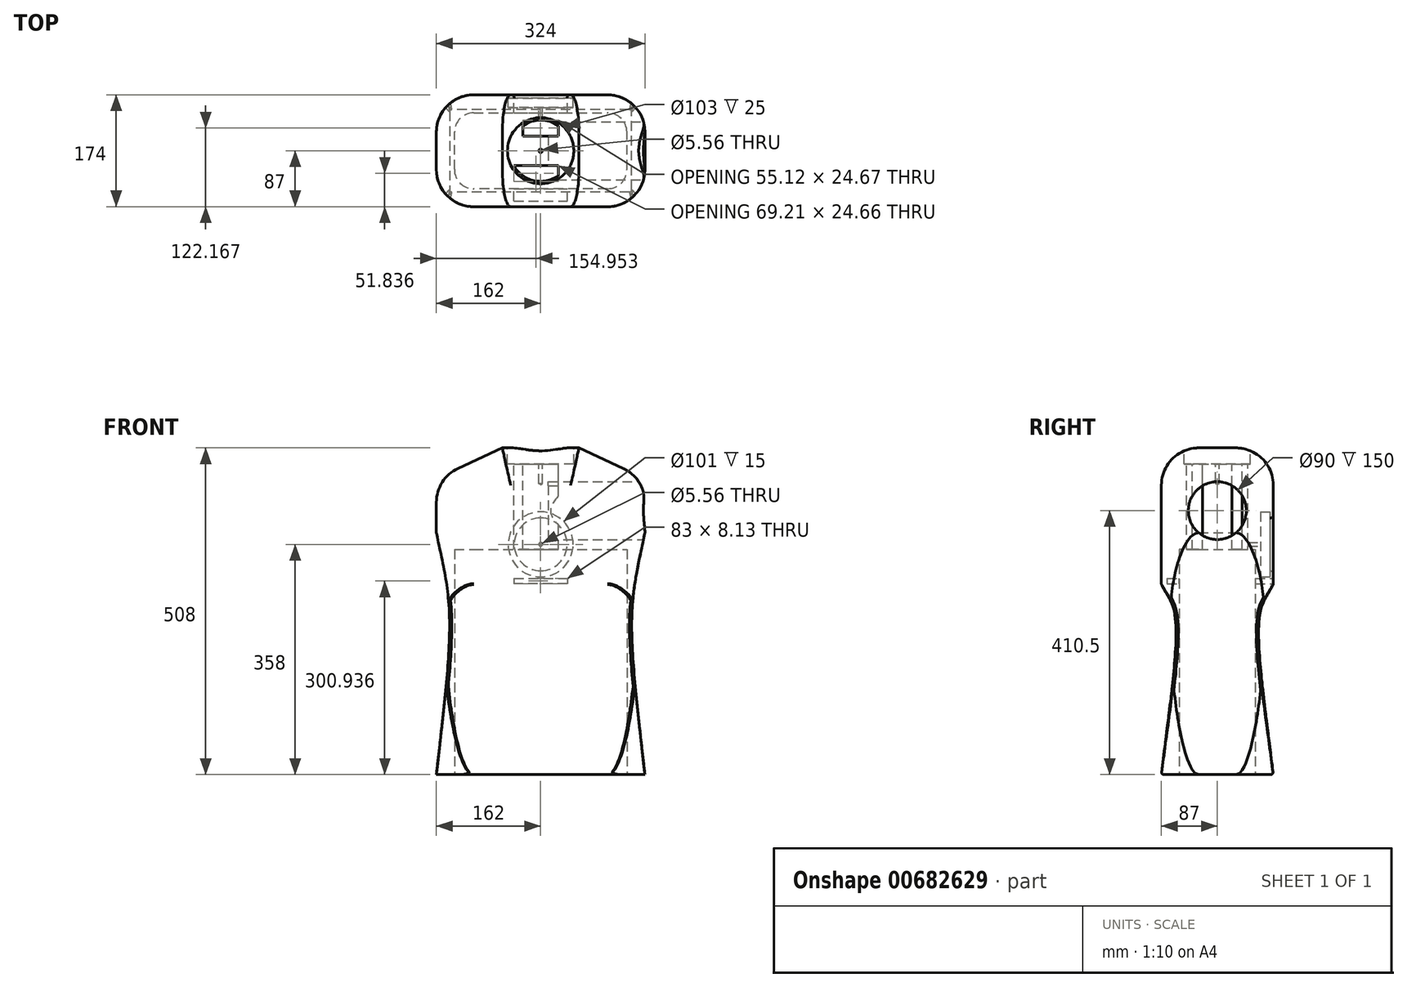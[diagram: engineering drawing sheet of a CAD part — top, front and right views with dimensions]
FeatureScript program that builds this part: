
annotation { "Feature Type Name" : "Feature", "Feature Type Description" : "" }
export const myFeature = defineFeature(function(context is Context, id is Id, definition is map)
    precondition{}
    {
        {
            var Q0;
            Q0=qCreatedBy(makeId("Front.planeOp"),FACE);
            var sketch = newSketch(context, id + "F0", { "sketchPlane" : qUnion([Q0])});
            skLineSegment(sketch, "E0.bottom", {"start": v(162, 254) * mm, "end": v(-162, 254) * mm});
            skLineSegment(sketch, "E0.top", {"start": v(162, -254) * mm, "end": v(-162, -254) * mm});
            skLineSegment(sketch, "E0.left", {"start": v(162, 254) * mm, "end": v(162, -254) * mm});
            skLineSegment(sketch, "E0.right", {"start": v(-162, 254) * mm, "end": v(-162, -254) * mm});
            skPoint(sketch, "E0.middle", {"position": v(0, 0) * mm});
            skSolve(sketch);
        }
        {
            var Q0;
            Q0=makeQuery(id+"F0.imprint","IMPRINT",FACE,{"disambiguationData":[TD([[makeQuery(id+"F0.imprint","IMPRINT",EDGE,{"derivedFrom":sQuery(id+"F0.wireOp",EDGE,"E0.bottom")}),1.0]])]});
            extrude(context, id + "F1", {"entities" : qUnion([Q0]), "depth" : 87 * mm, "offsetDistance" : 25 * mm, "hasSecondDirection" : true, "secondDirectionOppositeDirection" : true, "secondDirectionDepth" : 87 * mm});
        }
        {
            var Q0;
            Q0=makeQuery(id+"F1.opExtrude","SWEPT_FACE",FACE,{"disambiguationData":[OSD([sQuery(id+"F0.wireOp",EDGE,"E0.bottom")])]});
            var sketch = newSketch(context, id + "F2", { "sketchPlane" : qUnion([Q0])});
            skCircle(sketch, "E1", {"center": v(0, 0) * mm, "radius": 51.5 * mm});
            skPoint(sketch, "E1.centerSnap0", {"position": v(-162, 0) * mm});
            skPoint(sketch, "E1.centerSnap1", {"position": v(0, 87) * mm});
            skSolve(sketch);
        }
        {
            var Q0;
            Q0=makeQuery(id+"F2.imprint","IMPRINT",FACE,{"disambiguationData":[TD([[makeQuery(id+"F2.imprint","IMPRINT",EDGE,{"derivedFrom":sQuery(id+"F2.wireOp",EDGE,"E1")}),1.0]])]});
            extrude(context, id + "F3", {"entities" : qUnion([Q0]), "operationType" : NewBodyOperationType.REMOVE, "oppositeDirection" : true, "depth" : 25 * mm, "offsetDistance" : 25 * mm});
        }
        {
            var Q0;
            Q0=makeQuery(id+"F3.boolean.opBoolean","COPY",FACE,{"derivedFrom":makeQuery(id+"F3.opExtrude","CAP_FACE",FACE,{"disambiguationData":[OSD([sQuery(id+"F2.wireOp",EDGE,"E1")])],"isStart":false})});
            var sketch = newSketch(context, id + "F4", { "sketchPlane" : qUnion([Q0])});
            skCircle(sketch, "E2.0.0", {"center": v(0, 0) * mm, "radius": 51.5 * mm});
            skCircle(sketch, "E3", {"center": v(0, 0) * mm, "radius": 3.17 * mm});
            skSolve(sketch);
        }
        {
            var Q0;
            Q0=sQuery(id+"F4.wireOp",VERTEX,"E2.0.0.center");
            var Q1;
            Q1=makeQuery(id+"F1.opExtrude","SWEPT_BODY",BODY,{"disambiguationData":[OSD([sQuery(id+"F0.wireOp",EDGE,"E0.bottom"),sQuery(id+"F0.wireOp",EDGE,"E0.top"),sQuery(id+"F0.wireOp",EDGE,"E0.left"),sQuery(id+"F0.wireOp",EDGE,"E0.right")])]});
            hole(context, id + "F5", {"style" : HoleStyle.SIMPLE, "endStyle" : HoleEndStyle.BLIND, "standardTappedOrClearance" : lookupTablePath({ "standard" : "ANSI", "engagement" : "50%", "pitch" : "20 tpi", "size" : "1/4", "type" : "Tapped" }), "standardBlindInLast" : lookupTablePath({ "standard" : "ANSI", "engagement" : "50%", "pitch" : "20 tpi", "size" : "1/4", "type" : "Tapped" }), "holeDiameter" : 5.56 * mm, "majorDiameter" : 6.35 * mm, "showTappedDepth" : true, "holeDepth" : 30.48 * mm, "isTappedThrough" : true, "tappedDepth" : 25.4 * mm, "tapClearance" : 4, "locations" : qUnion([Q0]), "scope" : qUnion([Q1])});
        }
        {
            var Q0;
            Q0=makeQuery(id+"F1.opExtrude","SWEPT_EDGE",EDGE,{"disambiguationData":[OSD([sQuery(id+"F0.wireOp",EDGE,"E0.bottom"),sQuery(id+"F0.wireOp",EDGE,"E0.right")])]});
            var Q1;
            Q1=makeQuery(id+"F1.opExtrude","SWEPT_EDGE",EDGE,{"disambiguationData":[OSD([sQuery(id+"F0.wireOp",EDGE,"E0.bottom"),sQuery(id+"F0.wireOp",EDGE,"E0.left")])]});
            chamfer(context, id + "F6", {"entities" : qUnion([Q0, Q1]), "chamferType" : ChamferType.TWO_OFFSETS, "width1" : 47.5 * mm, "oppositeDirection" : false, "width2" : 102.5 * mm, "tangentPropagation" : true});
        }
        {
            var Q0;
            Q0=makeQuery(id+"F6.opChamfer","BLEND_FACE",FACE,{"disambiguationData":[OSD([sQuery(id+"F0.wireOp",EDGE,"E0.bottom"),sQuery(id+"F0.wireOp",EDGE,"E0.left")])]});
            var sketch = newSketch(context, id + "F7", { "sketchPlane" : qUnion([Q0])});
            skLineSegment(sketch, "E4.0.0", {"start": v(-52.81, -87) * mm, "end": v(60.16, -87) * mm});
            skLineSegment(sketch, "E4.0.1", {"start": v(60.16, -87) * mm, "end": v(60.16, 87) * mm});
            skLineSegment(sketch, "E4.0.2", {"start": v(60.16, 87) * mm, "end": v(-52.81, 87) * mm});
            skLineSegment(sketch, "E4.0.3", {"start": v(-52.81, 87) * mm, "end": v(-52.81, -87) * mm});
            skSolve(sketch);
        }
        {
            var Q0;
            {var subQ0=sQuery(id+"F0.wireOp",EDGE,"E0.right");var subQ1=sQuery(id+"F0.wireOp",EDGE,"E0.bottom");Q0=makeQuery(id+"F6.opChamfer","BLEND_EDGE",EDGE,{"blendedFrom":[makeQuery(id+"F1.opExtrude","SWEPT_EDGE",EDGE,{"disambiguationData":[OSD([subQ1,subQ0])]}),makeQuery(id+"F1.opExtrude","CAP_FACE",FACE,{"disambiguationData":[OSD([subQ1,sQuery(id+"F0.wireOp",EDGE,"E0.top"),sQuery(id+"F0.wireOp",EDGE,"E0.left"),subQ0])],"isStart":false})],"blendedInto":[makeQuery(id+"F1.opExtrude","CAP_FACE",FACE,{"disambiguationData":[OSD([subQ1,sQuery(id+"F0.wireOp",EDGE,"E0.top"),sQuery(id+"F0.wireOp",EDGE,"E0.left"),subQ0])],"isStart":false})]});}
            var Q1;
            Q1=makeQuery(id+"F1.opExtrude","CAP_EDGE",EDGE,{"disambiguationData":[OSD([sQuery(id+"F0.wireOp",EDGE,"E0.bottom")])],"isStart":false});
            var Q2;
            {var subQ0=sQuery(id+"F0.wireOp",EDGE,"E0.left");var subQ1=sQuery(id+"F0.wireOp",EDGE,"E0.bottom");Q2=makeQuery(id+"F6.opChamfer","BLEND_EDGE",EDGE,{"blendedFrom":[makeQuery(id+"F1.opExtrude","SWEPT_EDGE",EDGE,{"disambiguationData":[OSD([subQ1,subQ0])]}),makeQuery(id+"F1.opExtrude","CAP_FACE",FACE,{"disambiguationData":[OSD([subQ1,sQuery(id+"F0.wireOp",EDGE,"E0.top"),subQ0,sQuery(id+"F0.wireOp",EDGE,"E0.right")])],"isStart":false})],"blendedInto":[makeQuery(id+"F1.opExtrude","CAP_FACE",FACE,{"disambiguationData":[OSD([subQ1,sQuery(id+"F0.wireOp",EDGE,"E0.top"),subQ0,sQuery(id+"F0.wireOp",EDGE,"E0.right")])],"isStart":false})]});}
            var Q3;
            Q3=makeQuery(id+"F1.opExtrude","CAP_EDGE",EDGE,{"disambiguationData":[OSD([sQuery(id+"F0.wireOp",EDGE,"E0.bottom")])],"isStart":true});
            var Q4;
            {var subQ0=sQuery(id+"F0.wireOp",EDGE,"E0.right");var subQ1=sQuery(id+"F0.wireOp",EDGE,"E0.bottom");Q4=makeQuery(id+"F6.opChamfer","BLEND_EDGE",EDGE,{"blendedFrom":[makeQuery(id+"F1.opExtrude","SWEPT_EDGE",EDGE,{"disambiguationData":[OSD([subQ1,subQ0])]}),makeQuery(id+"F1.opExtrude","CAP_FACE",FACE,{"disambiguationData":[OSD([subQ1,sQuery(id+"F0.wireOp",EDGE,"E0.top"),sQuery(id+"F0.wireOp",EDGE,"E0.left"),subQ0])],"isStart":true})],"blendedInto":[makeQuery(id+"F1.opExtrude","CAP_FACE",FACE,{"disambiguationData":[OSD([subQ1,sQuery(id+"F0.wireOp",EDGE,"E0.top"),sQuery(id+"F0.wireOp",EDGE,"E0.left"),subQ0])],"isStart":true})]});}
            var Q5;
            {var subQ0=sQuery(id+"F0.wireOp",EDGE,"E0.left");var subQ1=sQuery(id+"F0.wireOp",EDGE,"E0.bottom");Q5=makeQuery(id+"F6.opChamfer","BLEND_EDGE",EDGE,{"blendedFrom":[makeQuery(id+"F1.opExtrude","SWEPT_EDGE",EDGE,{"disambiguationData":[OSD([subQ1,subQ0])]}),makeQuery(id+"F1.opExtrude","CAP_FACE",FACE,{"disambiguationData":[OSD([subQ1,sQuery(id+"F0.wireOp",EDGE,"E0.top"),subQ0,sQuery(id+"F0.wireOp",EDGE,"E0.right")])],"isStart":true})],"blendedInto":[makeQuery(id+"F1.opExtrude","CAP_FACE",FACE,{"disambiguationData":[OSD([subQ1,sQuery(id+"F0.wireOp",EDGE,"E0.top"),subQ0,sQuery(id+"F0.wireOp",EDGE,"E0.right")])],"isStart":true})]});}
            var Q6;
            Q6=makeQuery(id+"F1.opExtrude","CAP_EDGE",EDGE,{"disambiguationData":[OSD([sQuery(id+"F0.wireOp",EDGE,"E0.right")])],"isStart":true});
            var Q7;
            Q7=makeQuery(id+"F1.opExtrude","CAP_EDGE",EDGE,{"disambiguationData":[OSD([sQuery(id+"F0.wireOp",EDGE,"E0.right")])],"isStart":false});
            var Q8;
            {var subQ0=sQuery(id+"F0.wireOp",EDGE,"E0.right");Q8=makeQuery(id+"F6.opChamfer","BLEND_EDGE",EDGE,{"blendedFrom":[makeQuery(id+"F1.opExtrude","SWEPT_EDGE",EDGE,{"disambiguationData":[OSD([sQuery(id+"F0.wireOp",EDGE,"E0.bottom"),subQ0])]}),makeQuery(id+"F1.opExtrude","SWEPT_FACE",FACE,{"disambiguationData":[OSD([subQ0])]})],"blendedInto":[makeQuery(id+"F1.opExtrude","SWEPT_FACE",FACE,{"disambiguationData":[OSD([subQ0])]})]});}
            var Q9;
            Q9=makeQuery(id+"F1.opExtrude","CAP_EDGE",EDGE,{"disambiguationData":[OSD([sQuery(id+"F0.wireOp",EDGE,"E0.left")])],"isStart":false});
            var Q10;
            Q10=makeQuery(id+"F1.opExtrude","CAP_EDGE",EDGE,{"disambiguationData":[OSD([sQuery(id+"F0.wireOp",EDGE,"E0.left")])],"isStart":true});
            var Q11;
            {var subQ0=sQuery(id+"F0.wireOp",EDGE,"E0.left");Q11=makeQuery(id+"F6.opChamfer","BLEND_EDGE",EDGE,{"blendedFrom":[makeQuery(id+"F1.opExtrude","SWEPT_EDGE",EDGE,{"disambiguationData":[OSD([sQuery(id+"F0.wireOp",EDGE,"E0.bottom"),subQ0])]}),makeQuery(id+"F1.opExtrude","SWEPT_FACE",FACE,{"disambiguationData":[OSD([subQ0])]})],"blendedInto":[makeQuery(id+"F1.opExtrude","SWEPT_FACE",FACE,{"disambiguationData":[OSD([subQ0])]})]});}
            fillet(context, id + "F8", {"entities" : qUnion([Q0, Q1, Q2, Q3, Q4, Q5, Q6, Q7, Q8, Q9, Q10, Q11]), "radius" : 174 * mm / 3, "tangentPropagation" : true, "allowEdgeOverflow" : false});
        }
        {
            var Q0;
            Q0=makeQuery(id+"F1.opExtrude","SWEPT_FACE",FACE,{"disambiguationData":[OSD([sQuery(id+"F0.wireOp",EDGE,"E0.left")])]});
            var sketch = newSketch(context, id + "F9", { "sketchPlane" : qUnion([Q0])});
            skCircle(sketch, "E5", {"center": v(0, 156.5) * mm, "radius": 45 * mm});
            skSolve(sketch);
        }
        {
            var Q0;
            Q0=makeQuery(id+"F9.imprint","IMPRINT",FACE,{"disambiguationData":[TD([[makeQuery(id+"F9.imprint","IMPRINT",EDGE,{"derivedFrom":sQuery(id+"F9.wireOp",EDGE,"E5")}),1.0]])]});
            extrude(context, id + "F10", {"entities" : qUnion([Q0]), "operationType" : NewBodyOperationType.REMOVE, "oppositeDirection" : true, "depth" : 150 * mm, "offsetDistance" : 25 * mm});
        }
        {
            var Q0;
            Q0=makeQuery(id+"F1.opExtrude","CAP_FACE",FACE,{"disambiguationData":[OSD([sQuery(id+"F0.wireOp",EDGE,"E0.bottom"),sQuery(id+"F0.wireOp",EDGE,"E0.top"),sQuery(id+"F0.wireOp",EDGE,"E0.left"),sQuery(id+"F0.wireOp",EDGE,"E0.right")])],"isStart":true});
            var sketch = newSketch(context, id + "F11", { "sketchPlane" : qUnion([Q0])});
            skCircle(sketch, "E6", {"center": v(0, 104) * mm, "radius": 50.5 * mm});
            skSolve(sketch);
        }
        {
            var Q0;
            Q0=makeQuery(id+"F11.imprint","IMPRINT",FACE,{"disambiguationData":[TD([[makeQuery(id+"F11.imprint","IMPRINT",EDGE,{"derivedFrom":sQuery(id+"F11.wireOp",EDGE,"E6")}),1.0]])]});
            extrude(context, id + "F12", {"entities" : qUnion([Q0]), "operationType" : NewBodyOperationType.REMOVE, "oppositeDirection" : true, "depth" : 20 * mm, "offsetDistance" : 25 * mm});
        }
        {
            var Q0;
            Q0=makeQuery(id+"F12.boolean.opBoolean","COPY",FACE,{"derivedFrom":makeQuery(id+"F12.opExtrude","CAP_FACE",FACE,{"disambiguationData":[OSD([sQuery(id+"F11.wireOp",EDGE,"E6")])],"isStart":false})});
            var sketch = newSketch(context, id + "F13", { "sketchPlane" : qUnion([Q0])});
            skCircle(sketch, "E7.0.0", {"center": v(0, 104) * mm, "radius": 50.5 * mm});
            skCircle(sketch, "E8", {"center": v(0, 104) * mm, "radius": 3.18 * mm});
            skSolve(sketch);
        }
        {
            var Q0;
            Q0=sQuery(id+"F13.wireOp",VERTEX,"E7.0.0.center");
            var Q1;
            Q1=makeQuery(id+"F1.opExtrude","SWEPT_BODY",BODY,{"disambiguationData":[OSD([sQuery(id+"F0.wireOp",EDGE,"E0.bottom"),sQuery(id+"F0.wireOp",EDGE,"E0.top"),sQuery(id+"F0.wireOp",EDGE,"E0.left"),sQuery(id+"F0.wireOp",EDGE,"E0.right")])]});
            hole(context, id + "F14", {"style" : HoleStyle.SIMPLE, "endStyle" : HoleEndStyle.BLIND, "standardTappedOrClearance" : lookupTablePath({ "standard" : "ANSI", "engagement" : "50%", "pitch" : "20 tpi", "size" : "1/4", "type" : "Tapped" }), "standardBlindInLast" : lookupTablePath({ "standard" : "ANSI", "engagement" : "50%", "pitch" : "20 tpi", "size" : "1/4", "type" : "Tapped" }), "holeDiameter" : 5.56 * mm, "majorDiameter" : 6.35 * mm, "showTappedDepth" : true, "holeDepth" : 30.48 * mm, "isTappedThrough" : true, "tappedDepth" : 25.4 * mm, "tapClearance" : 4, "locations" : qUnion([Q0]), "scope" : qUnion([Q1])});
        }
        {
            var Q0;
            Q0=makeQuery(id+"F1.opExtrude","CAP_FACE",FACE,{"disambiguationData":[OSD([sQuery(id+"F0.wireOp",EDGE,"E0.bottom"),sQuery(id+"F0.wireOp",EDGE,"E0.top"),sQuery(id+"F0.wireOp",EDGE,"E0.left"),sQuery(id+"F0.wireOp",EDGE,"E0.right")])],"isStart":true});
            var sketch = newSketch(context, id + "F15", { "sketchPlane" : qUnion([Q0])});
            skFitSpline(sketch, "E9.0.0", {"points": [v(-159.13, 195.95) * mm, v(-159.01, 194.8) * mm, v(-158.81, 192.48) * mm, v(-158.6, 188.96) * mm, v(-158.5, 185.98) * mm, v(-158.46, 183.56) * mm, v(-158.47, 181.16) * mm, v(-158.54, 178.18) * mm, v(-158.73, 174.66) * mm, v(-158.96, 171.76) * mm, v(-159.18, 169.47) * mm, v(-159.43, 167.2) * mm, v(-159.76, 164.44) * mm, v(-160.2, 161.26) * mm, v(-160.56, 158.73) * mm, v(-160.85, 156.77) * mm, v(-161.06, 155.33) * mm, v(-161.25, 153.94) * mm, v(-161.5, 152.15) * mm, v(-161.74, 150.04) * mm, v(-161.95, 147.72) * mm, v(-162, 146.3) * mm, v(-162, 145.63) * mm]});
            skLineSegment(sketch, "E9.0.1", {"start": v(-162, -254) * mm, "end": v(-162, 122.1) * mm});
            skLineSegment(sketch, "E9.0.2", {"start": v(-162, -254) * mm, "end": v(-104, -254) * mm});
            skLineSegment(sketch, "E9.0.3", {"start": v(-104, -254) * mm, "end": v(-104, 169.45) * mm});
            skLineSegment(sketch, "E9.0.4", {"start": v(-104, 169.45) * mm, "end": v(-160.26, 169.45) * mm});
            skLineSegment(sketch, "E10.0.0", {"start": v(162, -254) * mm, "end": v(162, 122.1) * mm});
            skFitSpline(sketch, "E10.0.1", {"points": [v(162, 145.63) * mm, v(162, 146.3) * mm, v(161.95, 147.72) * mm, v(161.74, 150.04) * mm, v(161.5, 152.15) * mm, v(161.25, 153.94) * mm, v(161.06, 155.33) * mm, v(160.85, 156.77) * mm, v(160.56, 158.73) * mm, v(160.2, 161.26) * mm, v(159.76, 164.44) * mm, v(159.43, 167.2) * mm, v(159.18, 169.47) * mm, v(158.96, 171.76) * mm, v(158.73, 174.66) * mm, v(158.54, 178.18) * mm, v(158.47, 181.16) * mm, v(158.46, 183.56) * mm, v(158.5, 185.98) * mm, v(158.6, 188.96) * mm, v(158.81, 192.48) * mm, v(159.01, 194.8) * mm, v(159.13, 195.95) * mm]});
            skLineSegment(sketch, "E10.0.2", {"start": v(160.26, 169.45) * mm, "end": v(104, 169.45) * mm});
            skLineSegment(sketch, "E10.0.3", {"start": v(104, -254) * mm, "end": v(104, 169.45) * mm});
            skLineSegment(sketch, "E10.0.4", {"start": v(104, -254) * mm, "end": v(162, -254) * mm});
            skPoint(sketch, "E11", {"position": v(-142, 0) * mm});
            skPoint(sketch, "E12", {"position": v(142, 0) * mm});
            skFitSpline(sketch, "E13", {"points": [v(-162, 122.1) * mm, v(-142, 0) * mm, v(-162, -254) * mm], "startDerivative": vector(64.9, -318.47) * mm, "endDerivative": vector(-58.3, -522.84) * mm});
            skFitSpline(sketch, "E14", {"points": [v(162, 122.1) * mm, v(142, 0) * mm, v(162, -254) * mm], "startDerivative": vector(-64.9, -318.47) * mm, "endDerivative": vector(58.3, -522.84) * mm});
            skSolve(sketch);
        }
        {
            var Q0;
            Q0=makeQuery(id+"F15.imprint","IMPRINT",FACE,{"disambiguationData":[TD([[makeQuery(id+"F15.imprint","IMPRINT",EDGE,{"derivedFrom":sQuery(id+"F15.wireOp",EDGE,"E9.0.1")}),-1.0]])]});
            var Q1;
            Q1=makeQuery(id+"F15.imprint","IMPRINT",FACE,{"disambiguationData":[TD([[makeQuery(id+"F15.imprint","IMPRINT",EDGE,{"derivedFrom":sQuery(id+"F15.wireOp",EDGE,"E10.0.0")}),1.0]])]});
            extrude(context, id + "F16", {"entities" : qUnion([Q0, Q1]), "operationType" : NewBodyOperationType.REMOVE, "endBound" : BoundingType.THROUGH_ALL, "oppositeDirection" : true, "depth" : 25 * mm, "offsetDistance" : 25 * mm});
        }
        {
            var Q0;
            Q0=qCreatedBy(makeId("Right.planeOp"),FACE);
            var sketch = newSketch(context, id + "F17", { "sketchPlane" : qUnion([Q0])});
            skFitSpline(sketch, "E15.0.1", {"points": [v(-58, 145.63) * mm, v(-57.4, 145.63) * mm, v(-56.2, 145.53) * mm, v(-54.75, 145.2) * mm, v(-53.6, 144.82) * mm, v(-52.5, 144.36) * mm, v(-51.17, 143.68) * mm, v(-49.68, 142.72) * mm, v(-48.26, 141.61) * mm, v(-46.94, 140.43) * mm, v(-45.3, 138.76) * mm, v(-43.4, 136.51) * mm, v(-41.32, 133.63) * mm, v(-39.45, 130.66) * mm, v(-37.16, 126.61) * mm, v(-34.63, 121.4) * mm, v(-32.42, 116.03) * mm, v(-30.8, 111.66) * mm, v(-29.66, 108.35) * mm, v(-28.58, 105.02) * mm, v(-27.23, 100.57) * mm, v(-25.68, 94.97) * mm, v(-23.48, 85.98) * mm, v(-21.17, 74.64) * mm, v(-18.96, 60.92) * mm, v(-17.23, 47.1) * mm, v(-15.9, 33.16) * mm, v(-15.1, 21.48) * mm, v(-14.62, 12.08) * mm, v(-14.23, 2.68) * mm, v(-13.94, -9.06) * mm, v(-13.83, -23.13) * mm, v(-13.97, -41.88) * mm, v(-14.58, -65.28) * mm, v(-15.93, -93.32) * mm, v(-17.56, -116.66) * mm, v(-19.18, -135.33) * mm, v(-20.56, -149.3) * mm, v(-22.13, -163.25) * mm, v(-23.89, -177.17) * mm, v(-25.88, -191.06) * mm, v(-28.13, -204.9) * mm, v(-30.26, -216.39) * mm, v(-32.17, -225.54) * mm, v(-33.71, -232.38) * mm, v(-35.39, -239.18) * mm, v(-37.22, -245.95) * mm, v(-39.26, -252.66) * mm, v(-41.17, -258.18) * mm, v(-42.88, -262.53) * mm, v(-44.27, -265.75) * mm, v(-45.8, -268.9) * mm, v(-47.5, -271.98) * mm, v(-49.1, -274.41) * mm, v(-50.38, -276) * mm, v(-51.16, -276.88) * mm, v(-51.99, -277.72) * mm, v(-52.87, -278.5) * mm, v(-53.84, -279.17) * mm, v(-54.6, -279.62) * mm, v(-55.4, -280) * mm, v(-56.24, -280.28) * mm, v(-57.11, -280.46) * mm, v(-57.7, -280.5) * mm, v(-58, -280.5) * mm]});
            skLineSegment(sketch, "E15.0.3", {"start": v(87, -254) * mm, "end": v(87, 42.1) * mm});
            skFitSpline(sketch, "E16.0.1", {"points": [v(-116, -280.5) * mm, v(-116.6, -280.5) * mm, v(-117.34, -280.4) * mm, v(-118.2, -280.13) * mm, v(-118.76, -279.92) * mm, v(-119.44, -279.6) * mm, v(-120.2, -279.15) * mm, v(-120.93, -278.63) * mm, v(-121.62, -278.06) * mm, v(-122.5, -277.25) * mm, v(-123.5, -276.17) * mm, v(-124.6, -274.78) * mm, v(-125.62, -273.32) * mm, v(-126.57, -271.82) * mm, v(-127.44, -270.29) * mm, v(-128.55, -268.22) * mm, v(-129.81, -265.58) * mm, v(-131.2, -262.36) * mm, v(-132.47, -259.08) * mm, v(-133.67, -255.77) * mm, v(-135.15, -251.3) * mm, v(-136.85, -245.7) * mm, v(-138.67, -238.94) * mm, v(-140.34, -232.15) * mm, v(-141.88, -225.33) * mm, v(-143.77, -216.21) * mm, v(-145.9, -204.77) * mm, v(-148.13, -190.97) * mm, v(-150.12, -177.12) * mm, v(-151.88, -163.22) * mm, v(-153.44, -149.28) * mm, v(-154.82, -135.33) * mm, v(-156.43, -116.73) * mm, v(-158.06, -93.46) * mm, v(-159.4, -65.53) * mm, v(-160.03, -42.22) * mm, v(-160.17, -23.57) * mm, v(-160.07, -9.57) * mm, v(-159.73, 4.44) * mm, v(-159.1, 18.46) * mm, v(-158.3, 30.16) * mm, v(-157.49, 39.52) * mm, v(-156.78, 46.55) * mm, v(-155.96, 53.57) * mm, v(-154.72, 62.88) * mm, v(-153.24, 72.14) * mm, v(-151.46, 81.35) * mm, v(-149.97, 88.2) * mm, v(-148.3, 95.01) * mm, v(-146.44, 101.76) * mm, v(-144.35, 108.45) * mm, v(-142.39, 113.93) * mm, v(-140.66, 118.26) * mm, v(-138.8, 122.55) * mm, v(-136.77, 126.74) * mm, v(-134.48, 130.79) * mm, v(-132.6, 133.74) * mm, v(-130.54, 136.6) * mm, v(-128.64, 138.83) * mm, v(-126.98, 140.5) * mm, v(-125.66, 141.68) * mm, v(-124.27, 142.75) * mm, v(-123.04, 143.54) * mm, v(-122, 144.1) * mm, v(-121.2, 144.49) * mm, v(-120.37, 144.83) * mm, v(-119.25, 145.2) * mm, v(-117.8, 145.53) * mm, v(-116.6, 145.63) * mm, v(-116, 145.63) * mm]});
            skLineSegment(sketch, "E16.0.5", {"start": v(-87, -254) * mm, "end": v(-87, 42.1) * mm});
            skPoint(sketch, "E17", {"position": v(67, 0) * mm});
            skPoint(sketch, "E18", {"position": v(-67, 0) * mm});
            skPoint(sketch, "E19", {"position": v(87, 42.1) * mm});
            skPoint(sketch, "E20", {"position": v(-87, 42.1) * mm});
            skFitSpline(sketch, "E21", {"points": [v(-87, 42.1) * mm, v(-67, 0) * mm, v(-87, -254) * mm], "startDerivative": vector(75.43, -162.03) * mm, "endDerivative": vector(-60.12, -492.86) * mm});
            skFitSpline(sketch, "E22", {"points": [v(87, 42.1) * mm, v(67, 0) * mm, v(87, -254) * mm], "startDerivative": vector(-75.43, -162.03) * mm, "endDerivative": vector(60.12, -492.86) * mm});
            skPoint(sketch, "E23.orphan", {"position": v(87, 169.45) * mm});
            skPoint(sketch, "E15.0.0.end.orphan", {"position": v(43.1, 169.45) * mm});
            skPoint(sketch, "E24.orphan", {"position": v(29, 122.1) * mm});
            skPoint(sketch, "E16.0.3.start.orphan", {"position": v(-43.1, 169.45) * mm});
            skPoint(sketch, "E25.orphan", {"position": v(-87, 169.45) * mm});
            skPoint(sketch, "E16.0.2.end.orphan", {"position": v(-116, 152.33) * mm});
            skPoint(sketch, "E26.orphan", {"position": v(-48.62, 105.72) * mm});
            skPoint(sketch, "E15.0.2.start.orphan", {"position": v(29, -254) * mm});
            skPoint(sketch, "E16.0.0.end.orphan", {"position": v(-29, -254) * mm});
            skSolve(sketch);
        }
        {
            var Q0;
            Q0 = qSketchRegion(id + "F17", true);
            extrude(context, id + "F18", {"entities" : qUnion([Q0]), "operationType" : NewBodyOperationType.REMOVE, "endBound" : BoundingType.THROUGH_ALL, "oppositeDirection" : true, "depth" : 25 * mm, "offsetDistance" : 25 * mm, "hasSecondDirection" : true, "secondDirectionBound" : SecondDirectionBoundingType.THROUGH_ALL, "secondDirectionOppositeDirection" : false, "secondDirectionDepth" : 25 * mm});
        }
        {
            var Q0;
            Q0=makeQuery(id+"F18.boolean.opBoolean","COPY",FACE,{"derivedFrom":makeQuery(id+"F18.opExtrude","SWEPT_FACE",FACE,{"disambiguationData":[OSD([sQuery(id+"F17.wireOp",EDGE,"E22")])]})});
            var Q1;
            Q1=makeQuery(id+"F18.boolean.opBoolean","COPY",FACE,{"derivedFrom":makeQuery(id+"F18.opExtrude","SWEPT_FACE",FACE,{"disambiguationData":[OSD([sQuery(id+"F17.wireOp",EDGE,"E21")])]})});
            fillet(context, id + "F19", {"entities" : qUnion([Q0, Q1]), "radius" : 3.5 * mm, "tangentPropagation" : true, "allowEdgeOverflow" : false});
        }
        {
            var Q0;
            Q0=qCreatedBy(makeId("Front.planeOp"),FACE);
            var sketch = newSketch(context, id + "F20", { "sketchPlane" : qUnion([Q0])});
            skLineSegment(sketch, "E27.bottom", {"start": v(162, 254) * mm, "end": v(-162, 254) * mm});
            skLineSegment(sketch, "E27.top", {"start": v(162, -254) * mm, "end": v(-162, -254) * mm});
            skLineSegment(sketch, "E27.left", {"start": v(162, 254) * mm, "end": v(162, -254) * mm});
            skLineSegment(sketch, "E27.right", {"start": v(-162, 254) * mm, "end": v(-162, -254) * mm});
            skPoint(sketch, "E28.0", {"position": v(-162, -254) * mm});
            skLineSegment(sketch, "E29", {"start": v(0, 254) * mm, "end": v(0, -254) * mm});
            skPoint(sketch, "E30", {"position": v(0, 0) * mm});
            skPoint(sketch, "E31", {"position": v(0, -254) * mm});
            skSolve(sketch);
        }
        {
            var Q0;
            Q0=makeQuery(id+"F1.opExtrude","SWEPT_FACE",FACE,{"disambiguationData":[OSD([sQuery(id+"F0.wireOp",EDGE,"E0.top")])]});
            var sketch = newSketch(context, id + "F21", { "sketchPlane" : qUnion([Q0])});
            skArc(sketch, "E32.0.0", {"start": v(-162, -29) * mm, "mid": v(-151.88, -61.74) * mm, "end": v(-125.05, -83.05) * mm});
            skLineSegment(sketch, "E32.0.1", {"start": v(-125.05, -83.05) * mm, "end": v(125.05, -83.05) * mm});
            skArc(sketch, "E32.0.2", {"start": v(125.05, -83.05) * mm, "mid": v(151.88, -61.74) * mm, "end": v(162, -29) * mm});
            skLineSegment(sketch, "E32.0.3", {"start": v(162, -29) * mm, "end": v(162, 29) * mm});
            skArc(sketch, "E32.0.4", {"start": v(162, 29) * mm, "mid": v(151.88, 61.74) * mm, "end": v(125.05, 83.05) * mm});
            skLineSegment(sketch, "E32.0.5", {"start": v(125.05, 83.05) * mm, "end": v(-125.05, 83.05) * mm});
            skArc(sketch, "E32.0.6", {"start": v(-125.05, 83.05) * mm, "mid": v(-151.88, 61.74) * mm, "end": v(-162, 29) * mm});
            skLineSegment(sketch, "E32.0.7", {"start": v(-162, 29) * mm, "end": v(-162, -29) * mm});
            skArc(sketch, "E33", {"start": v(-134, -29) * mm, "mid": v(-125.21, -50.21) * mm, "end": v(-104, -59) * mm});
            skArc(sketch, "E34", {"start": v(134, 29) * mm, "mid": v(125.21, 50.21) * mm, "end": v(104, 59) * mm});
            skLineSegment(sketch, "E35", {"start": v(-104, -59) * mm, "end": v(104, -59) * mm});
            skLineSegment(sketch, "E36", {"start": v(104, -59) * mm, "end": v(104, 59) * mm});
            skLineSegment(sketch, "E37", {"start": v(104, 59) * mm, "end": v(-104, 59) * mm});
            skLineSegment(sketch, "E38", {"start": v(-104, 59) * mm, "end": v(-104, -59) * mm});
            skLineSegment(sketch, "E39", {"start": v(-134, 29) * mm, "end": v(-134, -29) * mm});
            skLineSegment(sketch, "E40", {"start": v(134, 29) * mm, "end": v(134, -29) * mm});
            skArc(sketch, "E41.trimOffspring", {"start": v(104, -59) * mm, "mid": v(125.21, -50.21) * mm, "end": v(134, -29) * mm});
            skArc(sketch, "E42.trimOffspring", {"start": v(-104, 59) * mm, "mid": v(-125.21, 50.21) * mm, "end": v(-134, 29) * mm});
            skSolve(sketch);
        }
        {
            var Q0;
            Q0=makeQuery(id+"F21.imprint","IMPRINT",FACE,{"disambiguationData":[TD([[makeQuery(id+"F21.imprint","IMPRINT",EDGE,{"derivedFrom":sQuery(id+"F21.wireOp",EDGE,"E33")}),1.0]])]});
            var Q1;
            Q1=makeQuery(id+"F21.imprint","IMPRINT",FACE,{"disambiguationData":[TD([[makeQuery(id+"F21.imprint","IMPRINT",EDGE,{"derivedFrom":sQuery(id+"F21.wireOp",EDGE,"E35")}),1.0]])]});
            var Q2;
            Q2=makeQuery(id+"F21.imprint","IMPRINT",FACE,{"disambiguationData":[TD([[makeQuery(id+"F21.imprint","IMPRINT",EDGE,{"derivedFrom":sQuery(id+"F21.wireOp",EDGE,"E34")}),1.0]])]});
            extrude(context, id + "F22", {"entities" : qUnion([Q0, Q1, Q2]), "operationType" : NewBodyOperationType.REMOVE, "oppositeDirection" : true, "depth" : 350 * mm, "offsetDistance" : 25 * mm});
        }
        {
            var Q0;
            Q0=makeQuery(id+"F3.boolean.opBoolean","COPY",FACE,{"derivedFrom":makeQuery(id+"F3.opExtrude","CAP_FACE",FACE,{"disambiguationData":[OSD([sQuery(id+"F2.wireOp",EDGE,"E1")])],"isStart":false})});
            var sketch = newSketch(context, id + "F23", { "sketchPlane" : qUnion([Q0])});
            skLineSegment(sketch, "E43.bottom", {"start": v(-27.56, -22.83) * mm, "end": v(27.56, -22.83) * mm});
            skLineSegment(sketch, "E43.top", {"start": v(-27.56, 22.83) * mm, "end": v(27.56, 22.83) * mm});
            skLineSegment(sketch, "E43.left", {"start": v(-27.56, -22.83) * mm, "end": v(-27.56, 22.83) * mm});
            skLineSegment(sketch, "E43.right", {"start": v(27.56, -22.83) * mm, "end": v(27.56, 22.83) * mm});
            skPoint(sketch, "E43.middle", {"position": v(0, 0) * mm});
            skCircle(sketch, "E44", {"center": v(0, 0) * mm, "radius": 47.5 * mm});
            skLineSegment(sketch, "E45", {"start": v(-27.56, -22.83) * mm, "end": v(-41.65, -22.83) * mm});
            skLineSegment(sketch, "E46", {"start": v(27.56, -22.83) * mm, "end": v(27.56, -38.69) * mm});
            skLineSegment(sketch, "E47", {"start": v(-27.56, 22.83) * mm, "end": v(-27.56, 38.69) * mm});
            skLineSegment(sketch, "E48", {"start": v(27.56, 22.83) * mm, "end": v(27.56, 38.69) * mm});
            skSolve(sketch);
        }
        {
            var Q0;
            Q0=makeQuery(id+"F23.imprint","IMPRINT",FACE,{"disambiguationData":[TD([[makeQuery(id+"F23.imprint","IMPRINT",EDGE,{"derivedFrom":sQuery(id+"F23.wireOp",EDGE,"E43.bottom")}),-1.0]])]});
            var Q1;
            Q1=makeQuery(id+"F23.imprint","IMPRINT",FACE,{"disambiguationData":[TD([[makeQuery(id+"F23.imprint","IMPRINT",EDGE,{"derivedFrom":sQuery(id+"F23.wireOp",EDGE,"E43.top")}),1.0]])]});
            extrude(context, id + "F24", {"entities" : qUnion([Q0, Q1]), "operationType" : NewBodyOperationType.REMOVE, "endBound" : BoundingType.THROUGH_ALL, "oppositeDirection" : true, "depth" : 25 * mm, "offsetDistance" : 25 * mm});
        }
        {
            var Q0;
            Q0=makeQuery(id+"F1.opExtrude","CAP_FACE",FACE,{"disambiguationData":[OSD([sQuery(id+"F0.wireOp",EDGE,"E0.bottom"),sQuery(id+"F0.wireOp",EDGE,"E0.top"),sQuery(id+"F0.wireOp",EDGE,"E0.left"),sQuery(id+"F0.wireOp",EDGE,"E0.right")])],"isStart":true});
            var sketch = newSketch(context, id + "F25", { "sketchPlane" : qUnion([Q0])});
            skCircle(sketch, "E49.0.0", {"center": v(0, 104) * mm, "radius": 50.5 * mm});
            skCircle(sketch, "E50", {"center": v(0, 104) * mm, "radius": 41 * mm});
            skSolve(sketch);
        }
        {
            var Q0;
            Q0=makeQuery(id+"F25.imprint","IMPRINT",FACE,{"disambiguationData":[TD([[makeQuery(id+"F25.imprint","IMPRINT",EDGE,{"derivedFrom":sQuery(id+"F25.wireOp",EDGE,"E49.0.0")}),1.0]])]});
            extrude(context, id + "F26", {"entities" : qUnion([Q0]), "operationType" : NewBodyOperationType.ADD, "oppositeDirection" : true, "depth" : 5 * mm, "offsetDistance" : 25 * mm});
        }
        {
            var Q0;
            Q0=makeQuery(id+"F26.opExtrude","CAP_EDGE",EDGE,{"disambiguationData":[OSD([sQuery(id+"F25.wireOp",EDGE,"E50")])],"isStart":true});
            fillet(context, id + "F27", {"entities" : qUnion([Q0]), "radius" : 5 * mm, "tangentPropagation" : true, "allowEdgeOverflow" : false});
        }
        {
            var Q0;
            Q0=qCreatedBy(makeId("Front.planeOp"),FACE);
            var sketch = newSketch(context, id + "F28", { "sketchPlane" : qUnion([Q0])});
            skLineSegment(sketch, "E51.bottom", {"start": v(-25.4, 254) * mm, "end": v(25.4, 254) * mm});
            skLineSegment(sketch, "E51.top", {"start": v(-25.4, -254) * mm, "end": v(25.4, -254) * mm});
            skLineSegment(sketch, "E51.left", {"start": v(-25.4, 254) * mm, "end": v(-25.4, -254) * mm});
            skLineSegment(sketch, "E51.right", {"start": v(25.4, 254) * mm, "end": v(25.4, -254) * mm});
            skPoint(sketch, "E51.middle", {"position": v(0, 0) * mm});
            skSolve(sketch);
        }
        {
            var Q0;
            {var subQ0=sQuery(id+"F0.wireOp",EDGE,"E0.left");var subQ3=sQuery(id+"F0.wireOp",EDGE,"E0.right");var subQ4=sQuery(id+"F0.wireOp",EDGE,"E0.top");var subQ5=sQuery(id+"F0.wireOp",EDGE,"E0.bottom");var subQ6=makeQuery(id+"F1.opExtrude","CAP_FACE",FACE,{"disambiguationData":[OSD([subQ5,subQ4,subQ0,subQ3])],"isStart":true});var subQ8=sQuery(id+"F25.wireOp",EDGE,"E50");Q0=makeQuery(id+"FbrGJrM4AJ48bs7_1.boolean.opBoolean","SPLIT",FACE,{"disambiguationData":[TD([makeQuery(id+"FbrGJrM4AJ48bs7_1.opExtrude","SWEPT_FACE",FACE,{"disambiguationData":[OSD([sQuery(id+"F28.wireOp",EDGE,"E51.right")])]})])],"derivedFrom":makeQuery(id+"F26.boolean.opBoolean","MERGE",FACE,{"derivedFrom":[subQ6,makeQuery(id+"F26.opExtrude","CAP_FACE",FACE,{"disambiguationData":[OSD([sQuery(id+"F25.wireOp",EDGE,"E49.0.0"),subQ8])],"isStart":true})]})});}
            var sketch = newSketch(context, id + "F29", { "sketchPlane" : qUnion([Q0])});
            skLineSegment(sketch, "E52.bottom", {"start": v(41.5, 51) * mm, "end": v(-41.5, 51) * mm});
            skLineSegment(sketch, "E52.top", {"start": v(41.5, 41) * mm, "end": v(-41.5, 41) * mm});
            skLineSegment(sketch, "E52.left", {"start": v(41.5, 51) * mm, "end": v(41.5, 41) * mm});
            skLineSegment(sketch, "E52.right", {"start": v(-41.5, 51) * mm, "end": v(-41.5, 41) * mm});
            skPoint(sketch, "E52.middle", {"position": v(0, 46) * mm});
            skCircle(sketch, "E53.0", {"center": v(0, 104) * mm, "radius": 46 * mm});
            skLineSegment(sketch, "E54.0", {"start": v(-104, 42.87) * mm, "end": v(104, 42.87) * mm});
            skPoint(sketch, "E55", {"position": v(0, 58) * mm});
            skSolve(sketch);
        }
        {
            var Q0;
            Q0=makeQuery(id+"F29.imprint","IMPRINT",FACE,{"disambiguationData":[TD([[makeQuery(id+"F29.imprint","IMPRINT",EDGE,{"derivedFrom":sQuery(id+"F29.wireOp",EDGE,"E52.bottom")}),1.0]])]});
            extrude(context, id + "F30", {"entities" : qUnion([Q0]), "operationType" : NewBodyOperationType.REMOVE, "oppositeDirection" : true, "depth" : 165 * mm, "offsetDistance" : 25 * mm});
        }
    });
